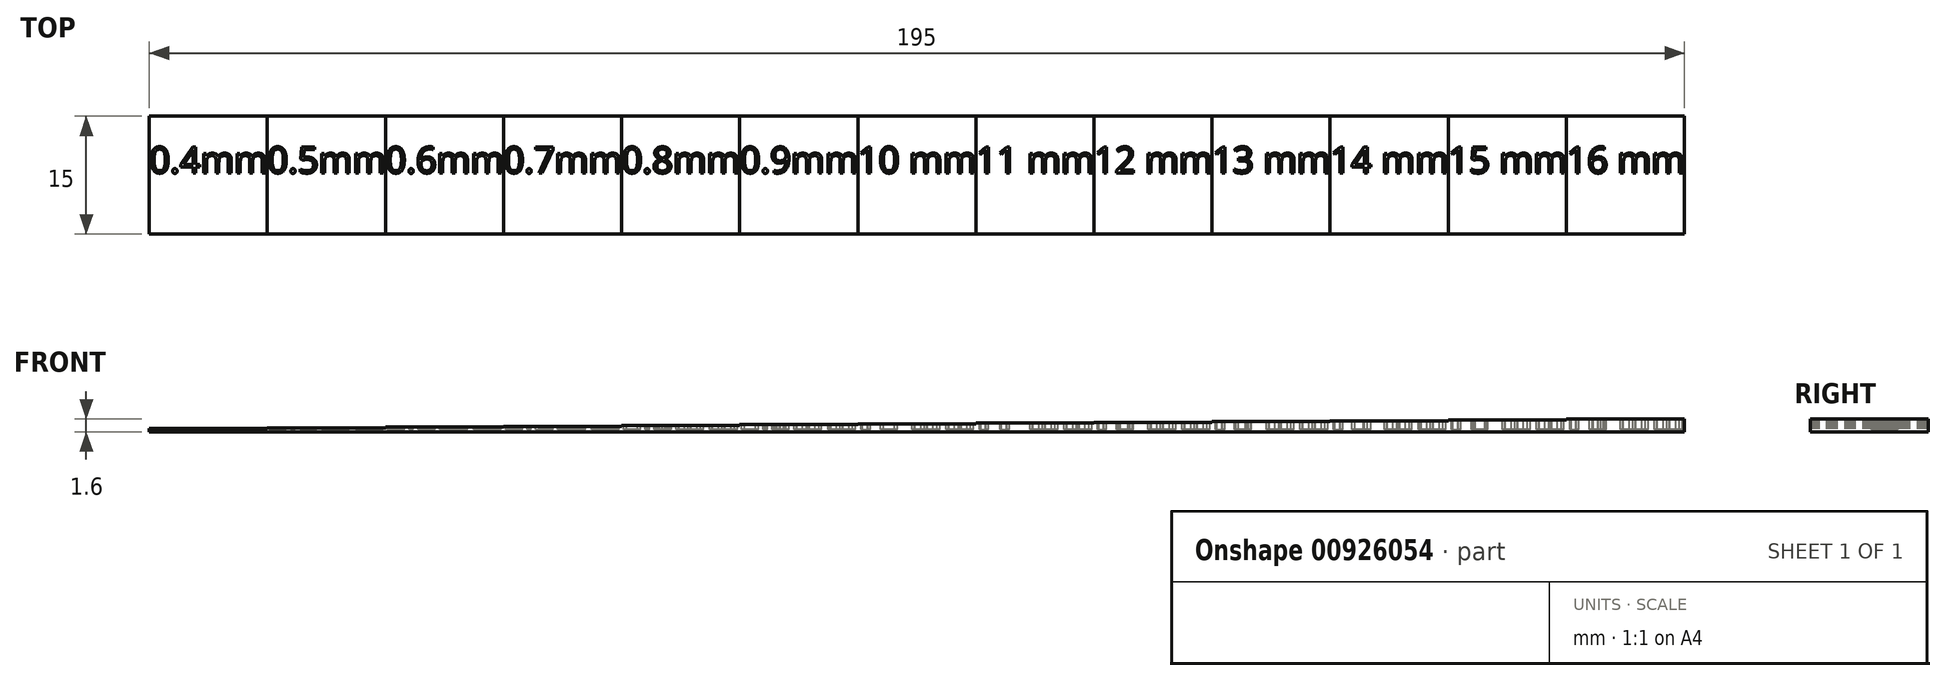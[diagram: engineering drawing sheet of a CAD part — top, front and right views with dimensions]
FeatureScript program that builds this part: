
annotation { "Feature Type Name" : "Feature", "Feature Type Description" : "" }
export const myFeature = defineFeature(function(context is Context, id is Id, definition is map)
    precondition{}
    {
        {
            var Q0;
            Q0=qCreatedBy(makeId("Top.planeOp"),FACE);
            var sketch = newSketch(context, id + "F0", { "sketchPlane" : qUnion([Q0])});
            skLineSegment(sketch, "E0.bottom", {"start": v(-84.87, 7.22) * mm, "end": v(110.13, 7.22) * mm});
            skLineSegment(sketch, "E0.top", {"start": v(-84.87, -7.78) * mm, "end": v(110.13, -7.78) * mm});
            skLineSegment(sketch, "E0.left", {"start": v(-84.87, 7.22) * mm, "end": v(-84.87, -7.78) * mm});
            skLineSegment(sketch, "E0.right", {"start": v(110.13, 7.22) * mm, "end": v(110.13, -7.78) * mm});
            skLineSegment(sketch, "E1", {"start": v(-69.87, 7.22) * mm, "end": v(-69.87, -7.78) * mm});
            skLineSegment(sketch, "E2", {"start": v(-54.87, 7.22) * mm, "end": v(-54.87, -7.78) * mm});
            skLineSegment(sketch, "E3", {"start": v(-39.87, 7.22) * mm, "end": v(-39.87, -7.78) * mm});
            skLineSegment(sketch, "E4", {"start": v(-24.87, 7.22) * mm, "end": v(-24.87, -7.78) * mm});
            skLineSegment(sketch, "E5", {"start": v(-9.87, 7.22) * mm, "end": v(-9.87, -7.78) * mm});
            skLineSegment(sketch, "E6", {"start": v(5.13, 7.22) * mm, "end": v(5.13, -7.78) * mm});
            skLineSegment(sketch, "E7", {"start": v(5.13, -7.78) * mm, "end": v(5.61, -7.44) * mm});
            skLineSegment(sketch, "E8", {"start": v(20.13, 7.22) * mm, "end": v(20.13, -7.78) * mm});
            skLineSegment(sketch, "E9", {"start": v(35.13, 7.22) * mm, "end": v(35.13, -7.78) * mm});
            skLineSegment(sketch, "E10", {"start": v(50.13, 7.22) * mm, "end": v(50.13, -7.78) * mm});
            skLineSegment(sketch, "E11", {"start": v(65.13, 7.22) * mm, "end": v(65.13, -7.78) * mm});
            skLineSegment(sketch, "E12", {"start": v(80.13, 7.22) * mm, "end": v(80.13, -7.78) * mm});
            skLineSegment(sketch, "E13", {"start": v(95.13, -7.78) * mm, "end": v(95.13, 7.22) * mm});
            skSolve(sketch);
        }
        {
            var Q0;
            {var subQ0=sQuery(id+"F0.wireOp",EDGE,"E0.left");Q0=makeQuery(id+"F0.imprint","IMPRINT",FACE,{"disambiguationData":[TD([[makeQuery(id+"F0.imprint","IMPRINT",EDGE,{"derivedFrom":subQ0}),1.0]])]});}
            extrude(context, id + "F1", {"entities" : qUnion([Q0]), "depth" : 0.4 * mm, "offsetDistance" : 25 * mm});
        }
        {
            var Q0;
            {var subQ0=sQuery(id+"F0.wireOp",EDGE,"E1");Q0=makeQuery(id+"F0.imprint","IMPRINT",FACE,{"disambiguationData":[TD([[makeQuery(id+"F0.imprint","IMPRINT",EDGE,{"derivedFrom":subQ0}),1.0]])]});}
            extrude(context, id + "F2", {"entities" : qUnion([Q0]), "operationType" : NewBodyOperationType.ADD, "depth" : 0.5 * mm, "offsetDistance" : 25 * mm});
        }
        {
            var Q0;
            {var subQ0=sQuery(id+"F0.wireOp",EDGE,"E2");Q0=makeQuery(id+"F0.imprint","IMPRINT",FACE,{"disambiguationData":[TD([[makeQuery(id+"F0.imprint","IMPRINT",EDGE,{"derivedFrom":subQ0}),1.0]])]});}
            extrude(context, id + "F3", {"entities" : qUnion([Q0]), "operationType" : NewBodyOperationType.ADD, "depth" : 0.6 * mm, "offsetDistance" : 25 * mm});
        }
        {
            var Q0;
            {var subQ0=sQuery(id+"F0.wireOp",EDGE,"E3");Q0=makeQuery(id+"F0.imprint","IMPRINT",FACE,{"disambiguationData":[TD([[makeQuery(id+"F0.imprint","IMPRINT",EDGE,{"derivedFrom":subQ0}),1.0]])]});}
            extrude(context, id + "F4", {"entities" : qUnion([Q0]), "operationType" : NewBodyOperationType.ADD, "depth" : 0.7 * mm, "offsetDistance" : 25 * mm});
        }
        {
            var Q0;
            {var subQ0=sQuery(id+"F0.wireOp",EDGE,"E4");Q0=makeQuery(id+"F0.imprint","IMPRINT",FACE,{"disambiguationData":[TD([[makeQuery(id+"F0.imprint","IMPRINT",EDGE,{"derivedFrom":subQ0}),1.0]])]});}
            extrude(context, id + "F5", {"entities" : qUnion([Q0]), "operationType" : NewBodyOperationType.ADD, "depth" : 0.8 * mm, "offsetDistance" : 25 * mm});
        }
        {
            var Q0;
            {var subQ0=sQuery(id+"F0.wireOp",EDGE,"E5");Q0=makeQuery(id+"F0.imprint","IMPRINT",FACE,{"disambiguationData":[TD([[makeQuery(id+"F0.imprint","IMPRINT",EDGE,{"derivedFrom":subQ0}),1.0]])]});}
            extrude(context, id + "F6", {"entities" : qUnion([Q0]), "operationType" : NewBodyOperationType.ADD, "depth" : 0.9 * mm, "offsetDistance" : 25 * mm});
        }
        {
            var Q0;
            {var subQ0=sQuery(id+"F0.wireOp",EDGE,"E6");Q0=makeQuery(id+"F0.imprint","IMPRINT",FACE,{"disambiguationData":[TD([[makeQuery(id+"F0.imprint","IMPRINT",EDGE,{"derivedFrom":subQ0}),1.0]])]});}
            extrude(context, id + "F7", {"entities" : qUnion([Q0]), "operationType" : NewBodyOperationType.ADD, "depth" : 1 * mm, "offsetDistance" : 25 * mm});
        }
        {
            var Q0;
            {var subQ0=sQuery(id+"F0.wireOp",EDGE,"E8");Q0=makeQuery(id+"F0.imprint","IMPRINT",FACE,{"disambiguationData":[TD([[makeQuery(id+"F0.imprint","IMPRINT",EDGE,{"derivedFrom":subQ0}),1.0]])]});}
            extrude(context, id + "F8", {"entities" : qUnion([Q0]), "operationType" : NewBodyOperationType.ADD, "depth" : 1.1 * mm, "offsetDistance" : 25 * mm});
        }
        {
            var Q0;
            {var subQ0=sQuery(id+"F0.wireOp",EDGE,"E9");Q0=makeQuery(id+"F0.imprint","IMPRINT",FACE,{"disambiguationData":[TD([[makeQuery(id+"F0.imprint","IMPRINT",EDGE,{"derivedFrom":subQ0}),1.0]])]});}
            extrude(context, id + "F9", {"entities" : qUnion([Q0]), "operationType" : NewBodyOperationType.ADD, "depth" : 1.2 * mm, "offsetDistance" : 25 * mm});
        }
        {
            var Q0;
            {var subQ0=sQuery(id+"F0.wireOp",EDGE,"E10");Q0=makeQuery(id+"F0.imprint","IMPRINT",FACE,{"disambiguationData":[TD([[makeQuery(id+"F0.imprint","IMPRINT",EDGE,{"derivedFrom":subQ0}),1.0]])]});}
            extrude(context, id + "F10", {"entities" : qUnion([Q0]), "operationType" : NewBodyOperationType.ADD, "depth" : 1.3 * mm, "offsetDistance" : 25 * mm});
        }
        {
            var Q0;
            {var subQ0=sQuery(id+"F0.wireOp",EDGE,"E11");Q0=makeQuery(id+"F0.imprint","IMPRINT",FACE,{"disambiguationData":[TD([[makeQuery(id+"F0.imprint","IMPRINT",EDGE,{"derivedFrom":subQ0}),1.0]])]});}
            extrude(context, id + "F11", {"entities" : qUnion([Q0]), "operationType" : NewBodyOperationType.ADD, "depth" : 1.4 * mm, "offsetDistance" : 25 * mm});
        }
        {
            var Q0;
            {var subQ0=sQuery(id+"F0.wireOp",EDGE,"E12");Q0=makeQuery(id+"F0.imprint","IMPRINT",FACE,{"disambiguationData":[TD([[makeQuery(id+"F0.imprint","IMPRINT",EDGE,{"derivedFrom":subQ0}),1.0]])]});}
            extrude(context, id + "F12", {"entities" : qUnion([Q0]), "operationType" : NewBodyOperationType.ADD, "depth" : 1.5 * mm, "offsetDistance" : 25 * mm});
        }
        {
            var Q0;
            {var subQ0=sQuery(id+"F0.wireOp",EDGE,"E0.right");Q0=makeQuery(id+"F0.imprint","IMPRINT",FACE,{"disambiguationData":[TD([[makeQuery(id+"F0.imprint","IMPRINT",EDGE,{"derivedFrom":subQ0}),-1.0]])]});}
            extrude(context, id + "F13", {"entities" : qUnion([Q0]), "operationType" : NewBodyOperationType.ADD, "depth" : 1.6 * mm, "offsetDistance" : 25 * mm});
        }
        {
            var Q0;
            Q0=makeQuery(id+"F1.opExtrude","CAP_FACE",FACE,{"disambiguationData":[OSD([sQuery(id+"F0.wireOp",EDGE,"E0.bottom"),sQuery(id+"F0.wireOp",EDGE,"E0.top"),sQuery(id+"F0.wireOp",EDGE,"E0.left"),sQuery(id+"F0.wireOp",EDGE,"E1")])],"isStart":false});
            var sketch = newSketch(context, id + "F14", { "sketchPlane" : qUnion([Q0])});
            skText(sketch, "E14", { "text": "0.4mm", "fontName": "OpenSans-Regular.ttf"});
            const initialGuessF14  = {"E14": [-0.08487, 0, 1, 0, 0.00332]};
            skSetInitialGuess(sketch, initialGuessF14);
            skSolve(sketch);
        }
        {
            var Q0;
            Q0 = qSketchRegion(id + "F14", true);
            extrude(context, id + "F15", {"entities" : qUnion([Q0]), "operationType" : NewBodyOperationType.REMOVE, "oppositeDirection" : true, "depth" : 0.1 * mm, "offsetDistance" : 25 * mm});
        }
        {
            var Q0;
            Q0=makeQuery(id+"F2.opExtrude","CAP_FACE",FACE,{"disambiguationData":[OSD([sQuery(id+"F0.wireOp",EDGE,"E0.bottom"),sQuery(id+"F0.wireOp",EDGE,"E0.top"),sQuery(id+"F0.wireOp",EDGE,"E1"),sQuery(id+"F0.wireOp",EDGE,"E2")])],"isStart":false});
            var sketch = newSketch(context, id + "F16", { "sketchPlane" : qUnion([Q0])});
            skText(sketch, "E15", { "text": "0.5mm", "fontName": "OpenSans-Regular.ttf"});
            const initialGuessF16  = {"E15": [-0.06987, 0, 1, 0, 0.00332]};
            skSetInitialGuess(sketch, initialGuessF16);
            skSolve(sketch);
        }
        {
            var Q0;
            Q0 = qSketchRegion(id + "F16", true);
            extrude(context, id + "F17", {"entities" : qUnion([Q0]), "operationType" : NewBodyOperationType.REMOVE, "oppositeDirection" : true, "depth" : 0.2 * mm, "offsetDistance" : 25 * mm});
        }
        {
            var Q0;
            Q0=makeQuery(id+"F3.opExtrude","CAP_FACE",FACE,{"disambiguationData":[OSD([sQuery(id+"F0.wireOp",EDGE,"E0.bottom"),sQuery(id+"F0.wireOp",EDGE,"E0.top"),sQuery(id+"F0.wireOp",EDGE,"E2"),sQuery(id+"F0.wireOp",EDGE,"E3")])],"isStart":false});
            var sketch = newSketch(context, id + "F18", { "sketchPlane" : qUnion([Q0])});
            skText(sketch, "E16", { "text": "0.6mm", "fontName": "OpenSans-Regular.ttf"});
            skPoint(sketch, "E16.secondSnap0", {"position": v(-39.87, -0.28) * mm});
            const initialGuessF18  = {"E16": [-0.05487, 0, 1, 0, 0.00332]};
            skSetInitialGuess(sketch, initialGuessF18);
            skSolve(sketch);
        }
        {
            var Q0;
            Q0 = qSketchRegion(id + "F18", true);
            extrude(context, id + "F19", {"entities" : qUnion([Q0]), "operationType" : NewBodyOperationType.REMOVE, "oppositeDirection" : true, "depth" : 0.3 * mm, "offsetDistance" : 25 * mm});
        }
        {
            var Q0;
            Q0=makeQuery(id+"F4.opExtrude","CAP_FACE",FACE,{"disambiguationData":[OSD([sQuery(id+"F0.wireOp",EDGE,"E0.bottom"),sQuery(id+"F0.wireOp",EDGE,"E0.top"),sQuery(id+"F0.wireOp",EDGE,"E3"),sQuery(id+"F0.wireOp",EDGE,"E4")])],"isStart":false});
            var sketch = newSketch(context, id + "F20", { "sketchPlane" : qUnion([Q0])});
            skText(sketch, "E17", { "text": "0.7mm", "fontName": "OpenSans-Regular.ttf"});
            const initialGuessF20  = {"E17": [-0.03987, 0, 1, 0, 0.00332]};
            skSetInitialGuess(sketch, initialGuessF20);
            skSolve(sketch);
        }
        {
            var Q0;
            Q0 = qSketchRegion(id + "F20", true);
            extrude(context, id + "F21", {"entities" : qUnion([Q0]), "operationType" : NewBodyOperationType.REMOVE, "oppositeDirection" : true, "depth" : 0.4 * mm, "offsetDistance" : 25 * mm});
        }
        {
            var Q0;
            Q0=makeQuery(id+"F5.opExtrude","CAP_FACE",FACE,{"disambiguationData":[OSD([sQuery(id+"F0.wireOp",EDGE,"E0.bottom"),sQuery(id+"F0.wireOp",EDGE,"E0.top"),sQuery(id+"F0.wireOp",EDGE,"E4"),sQuery(id+"F0.wireOp",EDGE,"E5")])],"isStart":false});
            var sketch = newSketch(context, id + "F22", { "sketchPlane" : qUnion([Q0])});
            skText(sketch, "E18", { "text": "0.8mm", "fontName": "OpenSans-Regular.ttf"});
            skPoint(sketch, "E18.secondSnap0", {"position": v(-9.87, -0.28) * mm});
            const initialGuessF22  = {"E18": [-0.02487, 0, 1, 0, 0.00332]};
            skSetInitialGuess(sketch, initialGuessF22);
            skSolve(sketch);
        }
        {
            var Q0;
            Q0 = qSketchRegion(id + "F22", true);
            extrude(context, id + "F23", {"entities" : qUnion([Q0]), "operationType" : NewBodyOperationType.REMOVE, "oppositeDirection" : true, "depth" : 0.5 * mm, "offsetDistance" : 25 * mm});
        }
        {
            var Q0;
            Q0=makeQuery(id+"F6.opExtrude","CAP_FACE",FACE,{"disambiguationData":[OSD([sQuery(id+"F0.wireOp",EDGE,"E0.bottom"),sQuery(id+"F0.wireOp",EDGE,"E0.top"),sQuery(id+"F0.wireOp",EDGE,"E5"),sQuery(id+"F0.wireOp",EDGE,"E6")])],"isStart":false});
            var sketch = newSketch(context, id + "F24", { "sketchPlane" : qUnion([Q0])});
            skText(sketch, "E19", { "text": "0.9mm", "fontName": "OpenSans-Regular.ttf"});
            skPoint(sketch, "E19.secondSnap0", {"position": v(5.13, -0.28) * mm});
            const initialGuessF24  = {"E19": [-0.00987, 0, 1, 0, 0.00332]};
            skSetInitialGuess(sketch, initialGuessF24);
            skSolve(sketch);
        }
        {
            var Q0;
            Q0 = qSketchRegion(id + "F24", true);
            extrude(context, id + "F25", {"entities" : qUnion([Q0]), "operationType" : NewBodyOperationType.REMOVE, "oppositeDirection" : true, "depth" : 0.6 * mm, "offsetDistance" : 25 * mm});
        }
        {
            var Q0;
            Q0=makeQuery(id+"F7.opExtrude","CAP_FACE",FACE,{"disambiguationData":[OSD([sQuery(id+"F0.wireOp",EDGE,"E0.bottom"),sQuery(id+"F0.wireOp",EDGE,"E0.top"),sQuery(id+"F0.wireOp",EDGE,"E6"),sQuery(id+"F0.wireOp",EDGE,"E8")])],"isStart":false});
            var sketch = newSketch(context, id + "F26", { "sketchPlane" : qUnion([Q0])});
            skText(sketch, "E20", { "text": "10 mm", "fontName": "OpenSans-Regular.ttf"});
            skPoint(sketch, "E20.secondSnap0", {"position": v(20.13, -0.28) * mm});
            const initialGuessF26  = {"E20": [0.00513, 0, 1, 0, 0.00333]};
            skSetInitialGuess(sketch, initialGuessF26);
            skSolve(sketch);
        }
        {
            var Q0;
            Q0 = qSketchRegion(id + "F26", true);
            extrude(context, id + "F27", {"entities" : qUnion([Q0]), "operationType" : NewBodyOperationType.REMOVE, "oppositeDirection" : true, "depth" : 0.7 * mm, "offsetDistance" : 25 * mm});
        }
        {
            var Q0;
            Q0=makeQuery(id+"F8.opExtrude","CAP_FACE",FACE,{"disambiguationData":[OSD([sQuery(id+"F0.wireOp",EDGE,"E0.bottom"),sQuery(id+"F0.wireOp",EDGE,"E0.top"),sQuery(id+"F0.wireOp",EDGE,"E8"),sQuery(id+"F0.wireOp",EDGE,"E9")])],"isStart":false});
            var sketch = newSketch(context, id + "F28", { "sketchPlane" : qUnion([Q0])});
            skText(sketch, "E21", { "text": "11 mm", "fontName": "OpenSans-Regular.ttf"});
            const initialGuessF28  = {"E21": [0.02013, 0, 1, 0, 0.00333]};
            skSetInitialGuess(sketch, initialGuessF28);
            skSolve(sketch);
        }
        {
            var Q0;
            Q0 = qSketchRegion(id + "F28", true);
            extrude(context, id + "F29", {"entities" : qUnion([Q0]), "operationType" : NewBodyOperationType.REMOVE, "oppositeDirection" : true, "depth" : 0.8 * mm, "offsetDistance" : 25 * mm});
        }
        {
            var Q0;
            Q0=makeQuery(id+"F9.opExtrude","CAP_FACE",FACE,{"disambiguationData":[OSD([sQuery(id+"F0.wireOp",EDGE,"E0.bottom"),sQuery(id+"F0.wireOp",EDGE,"E0.top"),sQuery(id+"F0.wireOp",EDGE,"E9"),sQuery(id+"F0.wireOp",EDGE,"E10")])],"isStart":false});
            var sketch = newSketch(context, id + "F30", { "sketchPlane" : qUnion([Q0])});
            skText(sketch, "E22", { "text": "12 mm", "fontName": "OpenSans-Regular.ttf"});
            const initialGuessF30  = {"E22": [0.03513, 0, 1, 0, 0.00333]};
            skSetInitialGuess(sketch, initialGuessF30);
            skSolve(sketch);
        }
        {
            var Q0;
            Q0 = qSketchRegion(id + "F30", true);
            extrude(context, id + "F31", {"entities" : qUnion([Q0]), "operationType" : NewBodyOperationType.REMOVE, "oppositeDirection" : true, "depth" : 0.9 * mm, "offsetDistance" : 25 * mm});
        }
        {
            var Q0;
            Q0=makeQuery(id+"F10.opExtrude","CAP_FACE",FACE,{"disambiguationData":[OSD([sQuery(id+"F0.wireOp",EDGE,"E0.bottom"),sQuery(id+"F0.wireOp",EDGE,"E0.top"),sQuery(id+"F0.wireOp",EDGE,"E10"),sQuery(id+"F0.wireOp",EDGE,"E11")])],"isStart":false});
            var sketch = newSketch(context, id + "F32", { "sketchPlane" : qUnion([Q0])});
            skText(sketch, "E23", { "text": "13 mm", "fontName": "OpenSans-Regular.ttf"});
            skPoint(sketch, "E23.secondSnap0", {"position": v(65.13, -0.28) * mm});
            const initialGuessF32  = {"E23": [0.05013, 0, 1, 0, 0.00333]};
            skSetInitialGuess(sketch, initialGuessF32);
            skSolve(sketch);
        }
        {
            var Q0;
            Q0 = qSketchRegion(id + "F32", true);
            extrude(context, id + "F33", {"entities" : qUnion([Q0]), "operationType" : NewBodyOperationType.REMOVE, "oppositeDirection" : true, "depth" : 1 * mm, "offsetDistance" : 25 * mm});
        }
        {
            var Q0;
            Q0=makeQuery(id+"F11.opExtrude","CAP_FACE",FACE,{"disambiguationData":[OSD([sQuery(id+"F0.wireOp",EDGE,"E0.bottom"),sQuery(id+"F0.wireOp",EDGE,"E0.top"),sQuery(id+"F0.wireOp",EDGE,"E11"),sQuery(id+"F0.wireOp",EDGE,"E12")])],"isStart":false});
            var sketch = newSketch(context, id + "F34", { "sketchPlane" : qUnion([Q0])});
            skText(sketch, "E24", { "text": "14 mm", "fontName": "OpenSans-Regular.ttf"});
            const initialGuessF34  = {"E24": [0.06513, 0, 1, 0, 0.00333]};
            skSetInitialGuess(sketch, initialGuessF34);
            skSolve(sketch);
        }
        {
            var Q0;
            Q0 = qSketchRegion(id + "F34", true);
            extrude(context, id + "F35", {"entities" : qUnion([Q0]), "operationType" : NewBodyOperationType.REMOVE, "oppositeDirection" : true, "depth" : 1.1 * mm, "offsetDistance" : 25 * mm});
        }
        {
            var Q0;
            Q0=makeQuery(id+"F12.opExtrude","CAP_FACE",FACE,{"disambiguationData":[OSD([sQuery(id+"F0.wireOp",EDGE,"E0.bottom"),sQuery(id+"F0.wireOp",EDGE,"E0.top"),sQuery(id+"F0.wireOp",EDGE,"E12"),sQuery(id+"F0.wireOp",EDGE,"E13")])],"isStart":false});
            var sketch = newSketch(context, id + "F36", { "sketchPlane" : qUnion([Q0])});
            skText(sketch, "E25", { "text": "15 mm", "fontName": "OpenSans-Regular.ttf"});
            const initialGuessF36  = {"E25": [0.08013, 0, 1, 0, 0.00333]};
            skSetInitialGuess(sketch, initialGuessF36);
            skSolve(sketch);
        }
        {
            var Q0;
            Q0 = qSketchRegion(id + "F36", true);
            extrude(context, id + "F37", {"entities" : qUnion([Q0]), "operationType" : NewBodyOperationType.REMOVE, "oppositeDirection" : true, "depth" : 1.2 * mm, "offsetDistance" : 25 * mm});
        }
        {
            var Q0;
            Q0=makeQuery(id+"F13.opExtrude","CAP_FACE",FACE,{"disambiguationData":[OSD([sQuery(id+"F0.wireOp",EDGE,"E0.bottom"),sQuery(id+"F0.wireOp",EDGE,"E0.top"),sQuery(id+"F0.wireOp",EDGE,"E0.right"),sQuery(id+"F0.wireOp",EDGE,"E13")])],"isStart":false});
            var sketch = newSketch(context, id + "F38", { "sketchPlane" : qUnion([Q0])});
            skText(sketch, "E26", { "text": "16 mm", "fontName": "OpenSans-Regular.ttf"});
            const initialGuessF38  = {"E26": [0.09513, 0, 1, 0, 0.00333]};
            skSetInitialGuess(sketch, initialGuessF38);
            skSolve(sketch);
        }
        {
            var Q0;
            Q0 = qSketchRegion(id + "F38", true);
            extrude(context, id + "F39", {"entities" : qUnion([Q0]), "operationType" : NewBodyOperationType.REMOVE, "oppositeDirection" : true, "depth" : 1.3 * mm, "offsetDistance" : 25 * mm});
        }
    });
